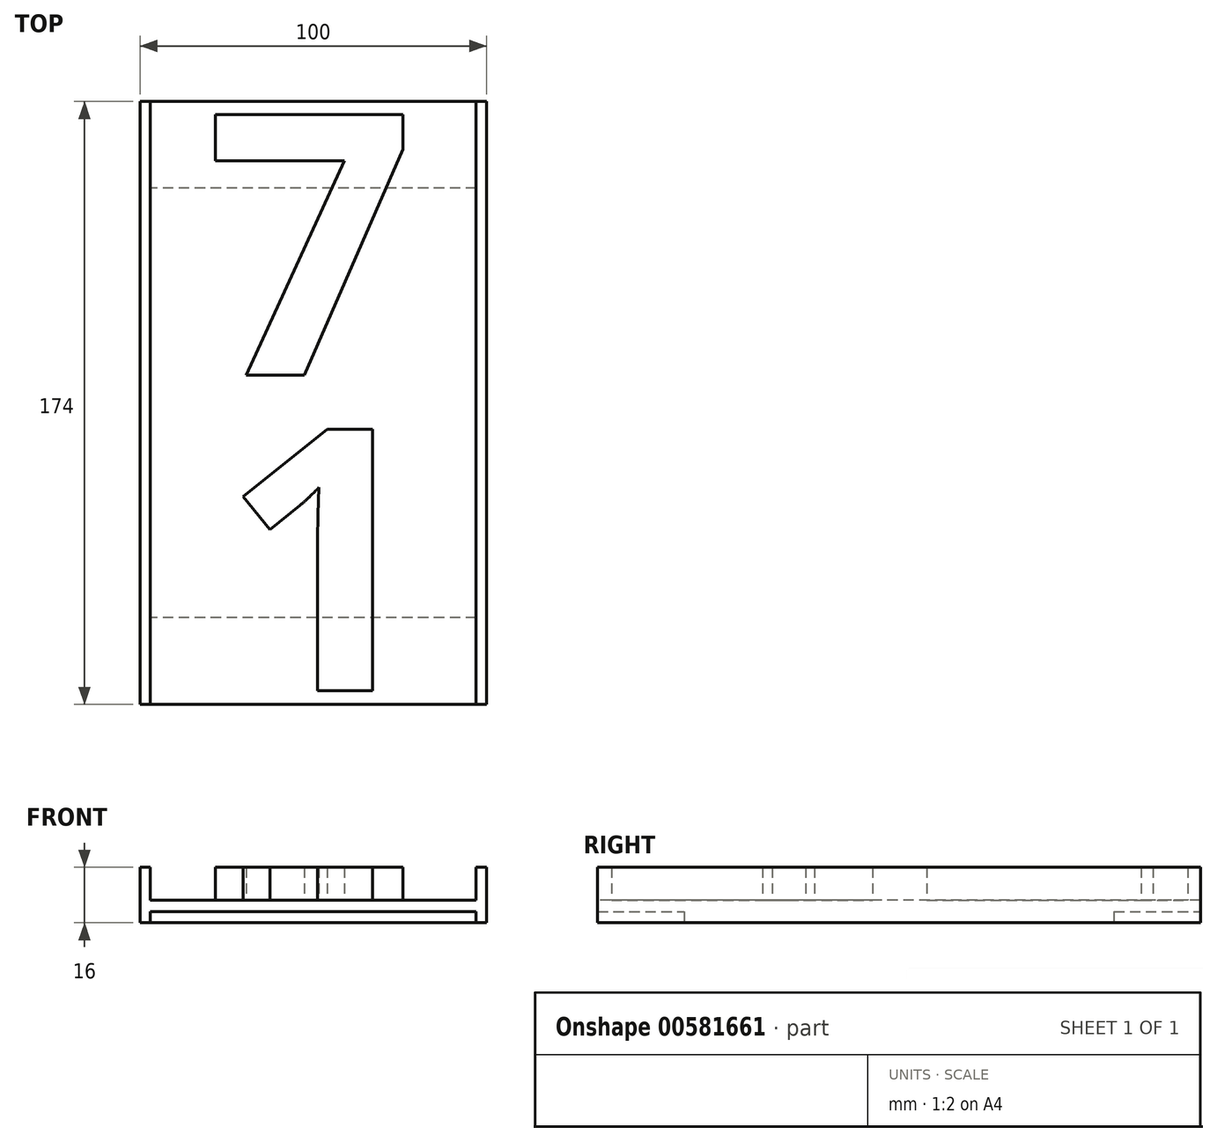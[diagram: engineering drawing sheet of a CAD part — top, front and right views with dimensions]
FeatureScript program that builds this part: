
annotation { "Feature Type Name" : "Feature", "Feature Type Description" : "" }
export const myFeature = defineFeature(function(context is Context, id is Id, definition is map)
    precondition{}
    {
        {
            var Q0;
            Q0=qCreatedBy(makeId("Top.planeOp"),FACE);
            var sketch = newSketch(context, id + "F0", { "sketchPlane" : qUnion([Q0])});
            skLineSegment(sketch, "E0.bottom", {"start": v(0, 0) * mm, "end": v(100, 0) * mm});
            skLineSegment(sketch, "E0.top", {"start": v(0, 177) * mm, "end": v(100, 177) * mm});
            skLineSegment(sketch, "E0.left", {"start": v(0, 0) * mm, "end": v(0, 177) * mm});
            skLineSegment(sketch, "E0.right", {"start": v(100, 0) * mm, "end": v(100, 177) * mm});
            skSolve(sketch);
        }
        {
            var Q0;
            Q0=qSketchRegion(id+"F0",true);
            extrude(context, id + "F1", {"entities" : qUnion([Q0]), "depth" : 16 * mm});
        }
        {
            var Q0;
            Q0=makeQuery(id+"F1.opExtrude","CAP_FACE",FACE,{"disambiguationData":[OSD([sQuery(id+"F0.wireOp",EDGE,"E0.bottom"),sQuery(id+"F0.wireOp",EDGE,"E0.top"),sQuery(id+"F0.wireOp",EDGE,"E0.left"),sQuery(id+"F0.wireOp",EDGE,"E0.right")])],"isStart":false});
            var sketch = newSketch(context, id + "F2", { "sketchPlane" : qUnion([Q0])});
            skLineSegment(sketch, "E1.bottom", {"start": v(3, 174) * mm, "end": v(97, 174) * mm});
            skLineSegment(sketch, "E1.top", {"start": v(3, -26) * mm, "end": v(97, -26) * mm});
            skLineSegment(sketch, "E1.left", {"start": v(3, 174) * mm, "end": v(3, -26) * mm});
            skLineSegment(sketch, "E1.right", {"start": v(97, 174) * mm, "end": v(97, -26) * mm});
            skSolve(sketch);
        }
        {
            var Q0;
            Q0=qSketchRegion(id+"F2",true);
            extrude(context, id + "F3", {"entities" : qUnion([Q0]), "operationType" : NewBodyOperationType.REMOVE, "oppositeDirection" : true, "depth" : 9.5 * mm});
        }
        {
            var Q0;
            Q0=makeQuery(id+"F1.opExtrude","CAP_FACE",FACE,{"disambiguationData":[OSD([sQuery(id+"F0.wireOp",EDGE,"E0.bottom"),sQuery(id+"F0.wireOp",EDGE,"E0.top"),sQuery(id+"F0.wireOp",EDGE,"E0.left"),sQuery(id+"F0.wireOp",EDGE,"E0.right")])],"isStart":true});
            var sketch = newSketch(context, id + "F4", { "sketchPlane" : qUnion([Q0])});
            skLineSegment(sketch, "E2.bottom", {"start": v(97, 3) * mm, "end": v(3, 3) * mm});
            skLineSegment(sketch, "E2.top", {"start": v(97, -25) * mm, "end": v(3, -25) * mm});
            skLineSegment(sketch, "E2.left", {"start": v(97, 3) * mm, "end": v(97, -25) * mm});
            skLineSegment(sketch, "E2.right", {"start": v(3, 3) * mm, "end": v(3, -25) * mm});
            skLineSegment(sketch, "E3.bottom", {"start": v(97, -149) * mm, "end": v(3, -149) * mm});
            skLineSegment(sketch, "E3.top", {"start": v(97, -177) * mm, "end": v(3, -177) * mm});
            skLineSegment(sketch, "E3.left", {"start": v(97, -149) * mm, "end": v(97, -177) * mm});
            skLineSegment(sketch, "E3.right", {"start": v(3, -149) * mm, "end": v(3, -177) * mm});
            skSolve(sketch);
        }
        {
            var Q0;
            Q0=qSketchRegion(id+"F4",true);
            extrude(context, id + "F5", {"entities" : qUnion([Q0]), "operationType" : NewBodyOperationType.REMOVE, "oppositeDirection" : true, "depth" : 3.2 * mm});
        }
        {
            var Q0;
            Q0=makeQuery(id+"F3.boolean.opBoolean","COPY",FACE,{"derivedFrom":makeQuery(id+"F3.opExtrude","CAP_FACE",FACE,{"disambiguationData":[OSD([sQuery(id+"F2.wireOp",EDGE,"E1.bottom"),sQuery(id+"F2.wireOp",EDGE,"E1.top"),sQuery(id+"F2.wireOp",EDGE,"E1.left"),sQuery(id+"F2.wireOp",EDGE,"E1.right")])],"isStart":false})});
            var sketch = newSketch(context, id + "F6", { "sketchPlane" : qUnion([Q0])});
            skText(sketch, "E4", { "text": "7", "fontName": "OpenSans-Bold.ttf"});
            skText(sketch, "E5", { "text": "1", "fontName": "OpenSans-Bold.ttf"});
            const initialGuessF6  = {"E4": [0.01895, 0.095, 1, 0, 0.076], "E5": [0.02355, 0.004, 1, 0, 0.076]};
            skSetInitialGuess(sketch, initialGuessF6);
            skSolve(sketch);
        }
        {
            var Q0;
            Q0=qSketchRegion(id+"F6",true);
            extrude(context, id + "F7", {"entities" : qUnion([Q0]), "operationType" : NewBodyOperationType.ADD, "depth" : 9.5 * mm});
        }
        {
            var Q0;
            Q0=makeQuery(id+"F1.opExtrude","SWEPT_FACE",FACE,{"disambiguationData":[OSD([sQuery(id+"F0.wireOp",EDGE,"E0.top")])]});
            var sketch = newSketch(context, id + "F8", { "sketchPlane" : qUnion([Q0])});
            skLineSegment(sketch, "E6.bottom", {"start": v(0, 0) * mm, "end": v(-100, 0) * mm});
            skLineSegment(sketch, "E6.top", {"start": v(0, 16) * mm, "end": v(-100, 16) * mm});
            skLineSegment(sketch, "E6.left", {"start": v(0, 0) * mm, "end": v(0, 16) * mm});
            skLineSegment(sketch, "E6.right", {"start": v(-100, 0) * mm, "end": v(-100, 16) * mm});
            skSolve(sketch);
        }
        {
            var Q0;
            Q0=makeQuery(id+"F8.imprint","IMPRINT",FACE,{"disambiguationData":[TD([[makeQuery(id+"F8.imprint","IMPRINT",EDGE,{"derivedFrom":sQuery(id+"F8.wireOp",EDGE,"E6.bottom")}),-1.0]])]});
            extrude(context, id + "F9", {"entities" : qUnion([Q0]), "operationType" : NewBodyOperationType.REMOVE, "oppositeDirection" : true, "depth" : 3 * mm, "offsetDistance" : 25 * mm});
        }
    });
